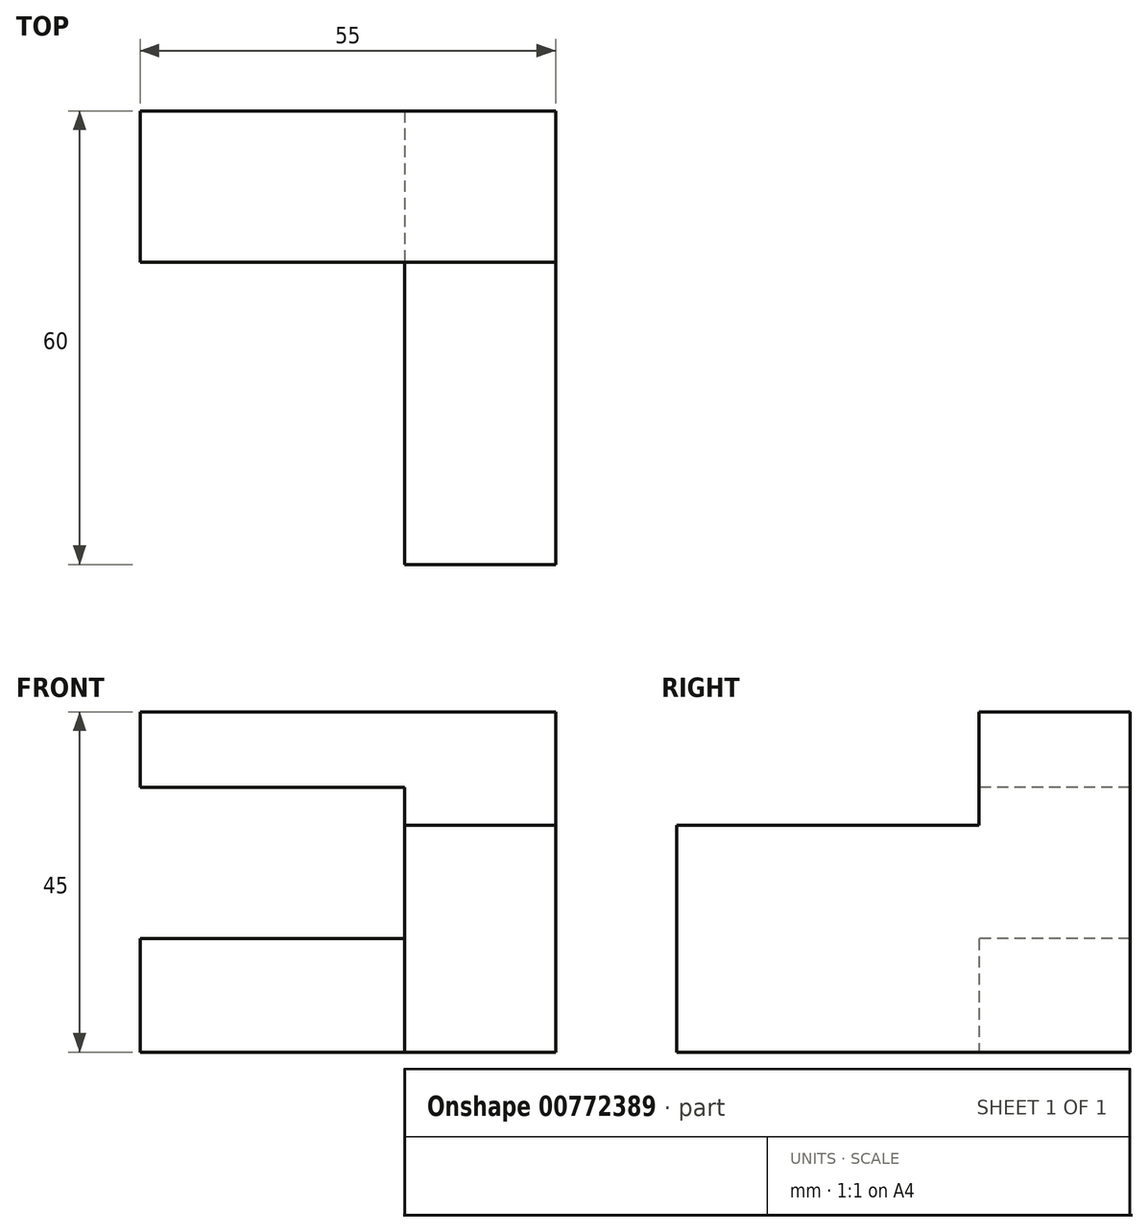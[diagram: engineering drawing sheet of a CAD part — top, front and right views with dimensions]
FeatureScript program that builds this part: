
annotation { "Feature Type Name" : "Feature", "Feature Type Description" : "" }
export const myFeature = defineFeature(function(context is Context, id is Id, definition is map)
    precondition{}
    {
        {
            var Q0;
            Q0=qCreatedBy(makeId("Front.planeOp"),FACE);
            var sketch = newSketch(context, id + "F0", { "sketchPlane" : qUnion([Q0])});
            skLineSegment(sketch, "E0", {"start": v(0, 0) * mm, "end": v(0, 45) * mm});
            skLineSegment(sketch, "E1", {"start": v(0, 45) * mm, "end": v(-55, 45) * mm});
            skLineSegment(sketch, "E2", {"start": v(-55, 45) * mm, "end": v(-55, 35) * mm});
            skLineSegment(sketch, "E3", {"start": v(-55, 35) * mm, "end": v(-20, 35) * mm});
            skLineSegment(sketch, "E4", {"start": v(-20, 35) * mm, "end": v(-20, 15) * mm});
            skLineSegment(sketch, "E5", {"start": v(-20, 15) * mm, "end": v(-55, 15) * mm});
            skLineSegment(sketch, "E6", {"start": v(-55, 15) * mm, "end": v(-55, 0) * mm});
            skLineSegment(sketch, "E7", {"start": v(-55, 0) * mm, "end": v(0, 0) * mm});
            skLineSegment(sketch, "E8", {"start": v(-20, 15) * mm, "end": v(-20, 0) * mm});
            skLineSegment(sketch, "E9", {"start": v(-20, 30) * mm, "end": v(0, 30) * mm});
            skSolve(sketch);
        }
        {
            var Q0;
            Q0=qSketchRegion(id+"F0",true);
            extrude(context, id + "F1", {"entities" : qUnion([Q0]), "oppositeDirection" : true, "depth" : 60 * mm, "offsetDistance" : 25 * mm});
        }
        {
            var Q0;
            {var subQ1=sQuery(id+"F0.wireOp",EDGE,"E1");Q0=makeQuery(id+"F0.imprint","IMPRINT",FACE,{"disambiguationData":[TD([[makeQuery(id+"F0.imprint","IMPRINT",EDGE,{"derivedFrom":subQ1}),1.0]])]});}
            extrude(context, id + "F2", {"entities" : qUnion([Q0]), "operationType" : NewBodyOperationType.REMOVE, "oppositeDirection" : true, "depth" : (60 - 20) * mm, "offsetDistance" : 25 * mm});
        }
        {
            var Q0;
            Q0=makeQuery(id+"F0.imprint","IMPRINT",FACE,{"disambiguationData":[TD([[makeQuery(id+"F0.imprint","IMPRINT",EDGE,{"derivedFrom":sQuery(id+"F0.wireOp",EDGE,"E5")}),1.0]])]});
            extrude(context, id + "F3", {"entities" : qUnion([Q0]), "operationType" : NewBodyOperationType.REMOVE, "oppositeDirection" : true, "depth" : (60 - 20) * mm, "offsetDistance" : 25 * mm});
        }
    });
